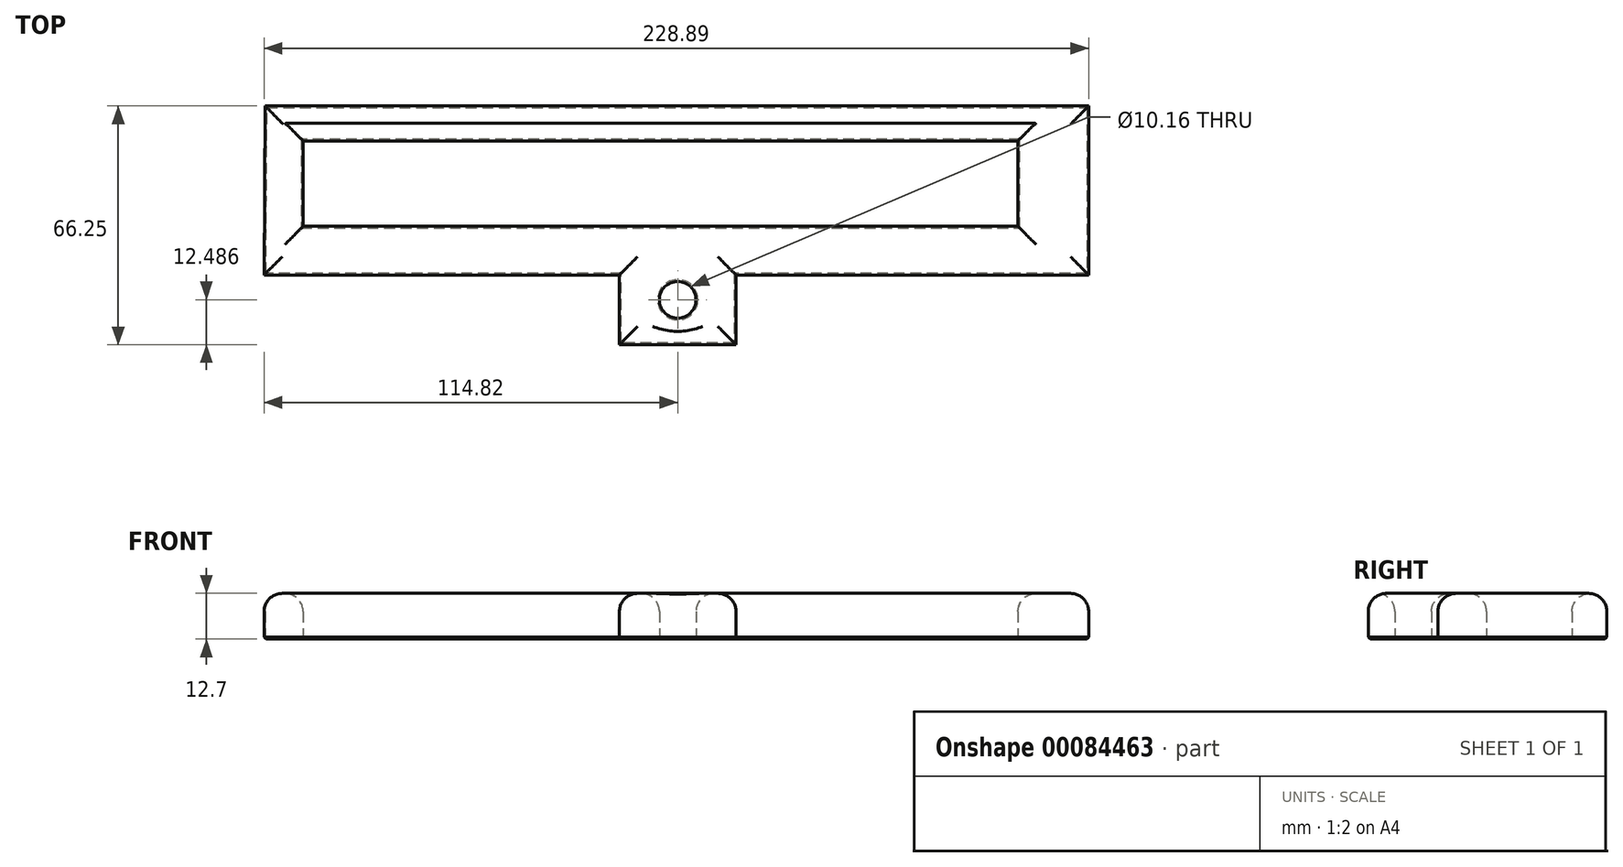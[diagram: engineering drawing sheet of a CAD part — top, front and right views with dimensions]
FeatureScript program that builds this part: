
annotation { "Feature Type Name" : "Feature", "Feature Type Description" : "" }
export const myFeature = defineFeature(function(context is Context, id is Id, definition is map)
    precondition{}
    {
        {
            var Q0;
            Q0=qCreatedBy(makeId("Top.planeOp"),FACE);
            var sketch = newSketch(context, id + "F0", { "sketchPlane" : qUnion([Q0])});
            skLineSegment(sketch, "E0", {"start": v(-114.53, 43.96) * mm, "end": v(114.07, 43.96) * mm});
            skLineSegment(sketch, "E1", {"start": v(-114.82, -2.93) * mm, "end": v(114.07, -2.93) * mm});
            skLineSegment(sketch, "E2", {"start": v(114.07, 43.96) * mm, "end": v(114.07, -2.93) * mm});
            skLineSegment(sketch, "E3", {"start": v(-114.53, 43.96) * mm, "end": v(-114.82, -2.93) * mm});
            skLineSegment(sketch, "E4", {"start": v(-103.98, 34.3) * mm, "end": v(94.44, 34.3) * mm});
            skLineSegment(sketch, "E5", {"start": v(94.44, 34.3) * mm, "end": v(94.44, 10.55) * mm});
            skLineSegment(sketch, "E6", {"start": v(94.44, 10.55) * mm, "end": v(-103.98, 10.55) * mm});
            skLineSegment(sketch, "E7", {"start": v(-103.98, 34.3) * mm, "end": v(-103.98, 10.55) * mm});
            skLineSegment(sketch, "E8", {"start": v(0, -22.29) * mm, "end": v(16.19, -22.29) * mm});
            skLineSegment(sketch, "E9", {"start": v(16.19, -22.29) * mm, "end": v(16.19, -2.93) * mm});
            skLineSegment(sketch, "E10.MirrorCS", {"start": v(-16.19, -22.29) * mm, "end": v(-16.19, -2.93) * mm});
            skLineSegment(sketch, "E11.MirrorCS", {"start": v(0, -22.29) * mm, "end": v(-16.19, -22.29) * mm});
            skSolve(sketch);
        }
        {
            var Q0;
            Q0=makeQuery(id+"F0.imprint","IMPRINT",FACE,{"disambiguationData":[TD([[makeQuery(id+"F0.imprint","IMPRINT",EDGE,{"derivedFrom":sQuery(id+"F0.wireOp",EDGE,"E8")}),1.0]])]});
            var sketch = newSketch(context, id + "F1", { "sketchPlane" : qUnion([Q0])});
            skCircle(sketch, "E12", {"center": v(0, -9.8) * mm, "radius": 5.08 * mm});
            skSolve(sketch);
        }
        {
            var Q0;
            Q0=makeQuery(id+"F1.imprint","IMPRINT",FACE,{"disambiguationData":[TD([[makeQuery(id+"F1.imprint","IMPRINT",EDGE,{"derivedFrom":sQuery(id+"F1.wireOp",EDGE,"E12")}),-1.0]])]});
            var Q1;
            Q1=makeQuery(id+"F0.imprint","IMPRINT",FACE,{"disambiguationData":[TD([[makeQuery(id+"F0.imprint","IMPRINT",EDGE,{"derivedFrom":sQuery(id+"F0.wireOp",EDGE,"E0")}),-1.0]])]});
            extrude(context, id + "F2", {"entities" : qUnion([Q0, Q1]), "depth" : 12.7 * mm});
        }
        {
            var Q0;
            Q0=makeQuery(id+"F2.opExtrude","SWEPT_BODY",BODY,{"disambiguationData":[OSD([sQuery(id+"F0.wireOp",EDGE,"E1"),sQuery(id+"F0.wireOp",EDGE,"E8"),sQuery(id+"F0.wireOp",EDGE,"E9"),sQuery(id+"F0.wireOp",EDGE,"E10.MirrorCS"),sQuery(id+"F0.wireOp",EDGE,"E11.MirrorCS"),sQuery(id+"F1.wireOp",EDGE,"E12")])]});
            var Q1;
            Q1=makeQuery(id+"F2.opExtrude","SWEPT_BODY",BODY,{"disambiguationData":[OSD([sQuery(id+"F0.wireOp",EDGE,"E0"),sQuery(id+"F0.wireOp",EDGE,"E1"),sQuery(id+"F0.wireOp",EDGE,"E2"),sQuery(id+"F0.wireOp",EDGE,"E3"),sQuery(id+"F0.wireOp",EDGE,"E4"),sQuery(id+"F0.wireOp",EDGE,"E5"),sQuery(id+"F0.wireOp",EDGE,"E6"),sQuery(id+"F0.wireOp",EDGE,"E7")])]});
            booleanBodies(context, id + "F3", {"operationType" : BooleanOperationType.UNION, "tools" : qUnion([Q0, Q1])});
        }
        {
            var Q0;
            {var subQ0=sQuery(id+"F0.wireOp",EDGE,"E1");Q0=makeQuery(id+"F3.opBoolean","MERGE",FACE,{"derivedFrom":[makeQuery(id+"F2.opExtrude","CAP_FACE",FACE,{"disambiguationData":[OSD([sQuery(id+"F0.wireOp",EDGE,"E0"),subQ0,sQuery(id+"F0.wireOp",EDGE,"E2"),sQuery(id+"F0.wireOp",EDGE,"E3"),sQuery(id+"F0.wireOp",EDGE,"E4"),sQuery(id+"F0.wireOp",EDGE,"E5"),sQuery(id+"F0.wireOp",EDGE,"E6"),sQuery(id+"F0.wireOp",EDGE,"E7")])],"isStart":false}),makeQuery(id+"F2.opExtrude","CAP_FACE",FACE,{"disambiguationData":[OSD([subQ0,sQuery(id+"F0.wireOp",EDGE,"E8"),sQuery(id+"F0.wireOp",EDGE,"E9"),sQuery(id+"F0.wireOp",EDGE,"E10.MirrorCS"),sQuery(id+"F0.wireOp",EDGE,"E11.MirrorCS"),sQuery(id+"F1.wireOp",EDGE,"E12")])],"isStart":false})]});}
            fillet(context, id + "F4", {"entities" : qUnion([Q0]), "radius" : 5.08 * mm, "tangentPropagation" : true, "allowEdgeOverflow" : false});
        }
        {
            var Q0;
            {var subQ0=sQuery(id+"F0.wireOp",EDGE,"E1");Q0=makeQuery(id+"F3.opBoolean","MERGE",FACE,{"derivedFrom":[makeQuery(id+"F2.opExtrude","CAP_FACE",FACE,{"disambiguationData":[OSD([sQuery(id+"F0.wireOp",EDGE,"E0"),subQ0,sQuery(id+"F0.wireOp",EDGE,"E2"),sQuery(id+"F0.wireOp",EDGE,"E3"),sQuery(id+"F0.wireOp",EDGE,"E4"),sQuery(id+"F0.wireOp",EDGE,"E5"),sQuery(id+"F0.wireOp",EDGE,"E6"),sQuery(id+"F0.wireOp",EDGE,"E7")])],"isStart":true}),makeQuery(id+"F2.opExtrude","CAP_FACE",FACE,{"disambiguationData":[OSD([subQ0,sQuery(id+"F0.wireOp",EDGE,"E8"),sQuery(id+"F0.wireOp",EDGE,"E9"),sQuery(id+"F0.wireOp",EDGE,"E10.MirrorCS"),sQuery(id+"F0.wireOp",EDGE,"E11.MirrorCS"),sQuery(id+"F1.wireOp",EDGE,"E12")])],"isStart":true})]});}
            chamfer(context, id + "F5", {"entities" : qUnion([Q0]), "width" : 0.5 * mm, "tangentPropagation" : true});
        }
    });
